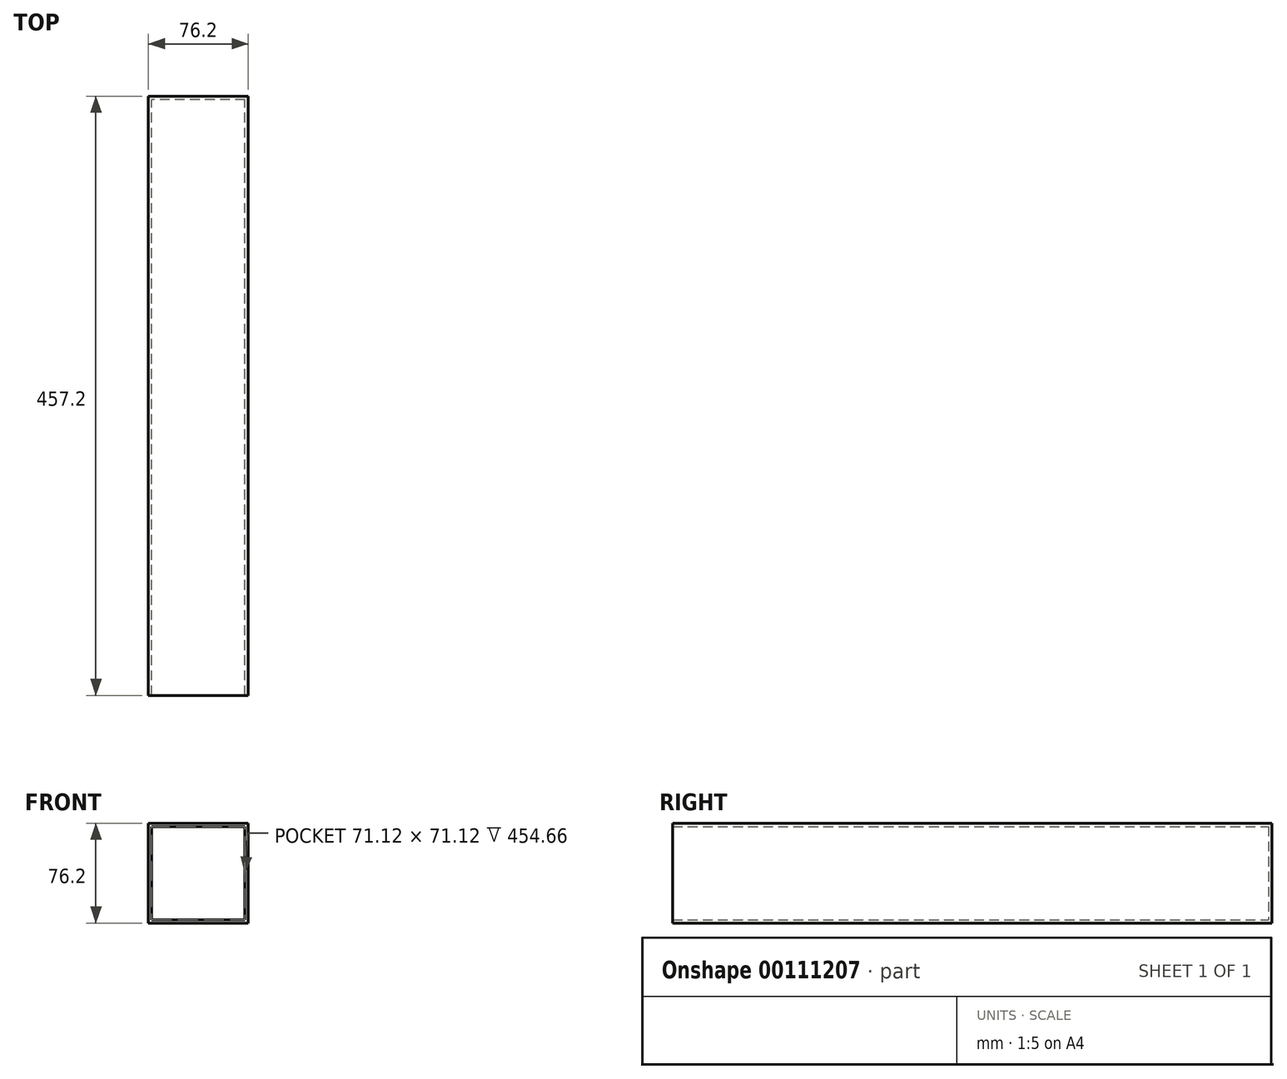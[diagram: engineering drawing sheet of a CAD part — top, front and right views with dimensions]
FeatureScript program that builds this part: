
annotation { "Feature Type Name" : "Feature", "Feature Type Description" : "" }
export const myFeature = defineFeature(function(context is Context, id is Id, definition is map)
    precondition{}
    {
        {
            var Q0;
            Q0=qCreatedBy(makeId("Front.planeOp"),FACE);
            var sketch = newSketch(context, id + "F0", { "sketchPlane" : qUnion([Q0])});
            skLineSegment(sketch, "E0.bottom", {"start": v(38.24, 38.1) * mm, "end": v(-37.96, 38.1) * mm});
            skLineSegment(sketch, "E0.top", {"start": v(38.24, -38.1) * mm, "end": v(-37.96, -38.1) * mm});
            skLineSegment(sketch, "E0.left", {"start": v(38.24, 38.1) * mm, "end": v(38.24, -38.1) * mm});
            skLineSegment(sketch, "E0.right", {"start": v(-37.96, 38.1) * mm, "end": v(-37.96, -38.1) * mm});
            skPoint(sketch, "E0.middle", {"position": v(0.14, 0) * mm});
            skSolve(sketch);
        }
        {
            var Q0;
            Q0 = qSketchRegion(id + "F0", true);
            extrude(context, id + "F1", {"entities" : qUnion([Q0]), "depth" : 457.2 * mm});
        }
        {
            var Q0;
            Q0=makeQuery(id+"F1.opExtrude","CAP_FACE",FACE,{"disambiguationData":[OSD([sQuery(id+"F0.wireOp",EDGE,"E0.bottom"),sQuery(id+"F0.wireOp",EDGE,"E0.top"),sQuery(id+"F0.wireOp",EDGE,"E0.left"),sQuery(id+"F0.wireOp",EDGE,"E0.right")])],"isStart":false});
            shell(context, id + "F2", {"entities" : qUnion([Q0]), "thickness" : 2.54 * mm});
        }
    });
